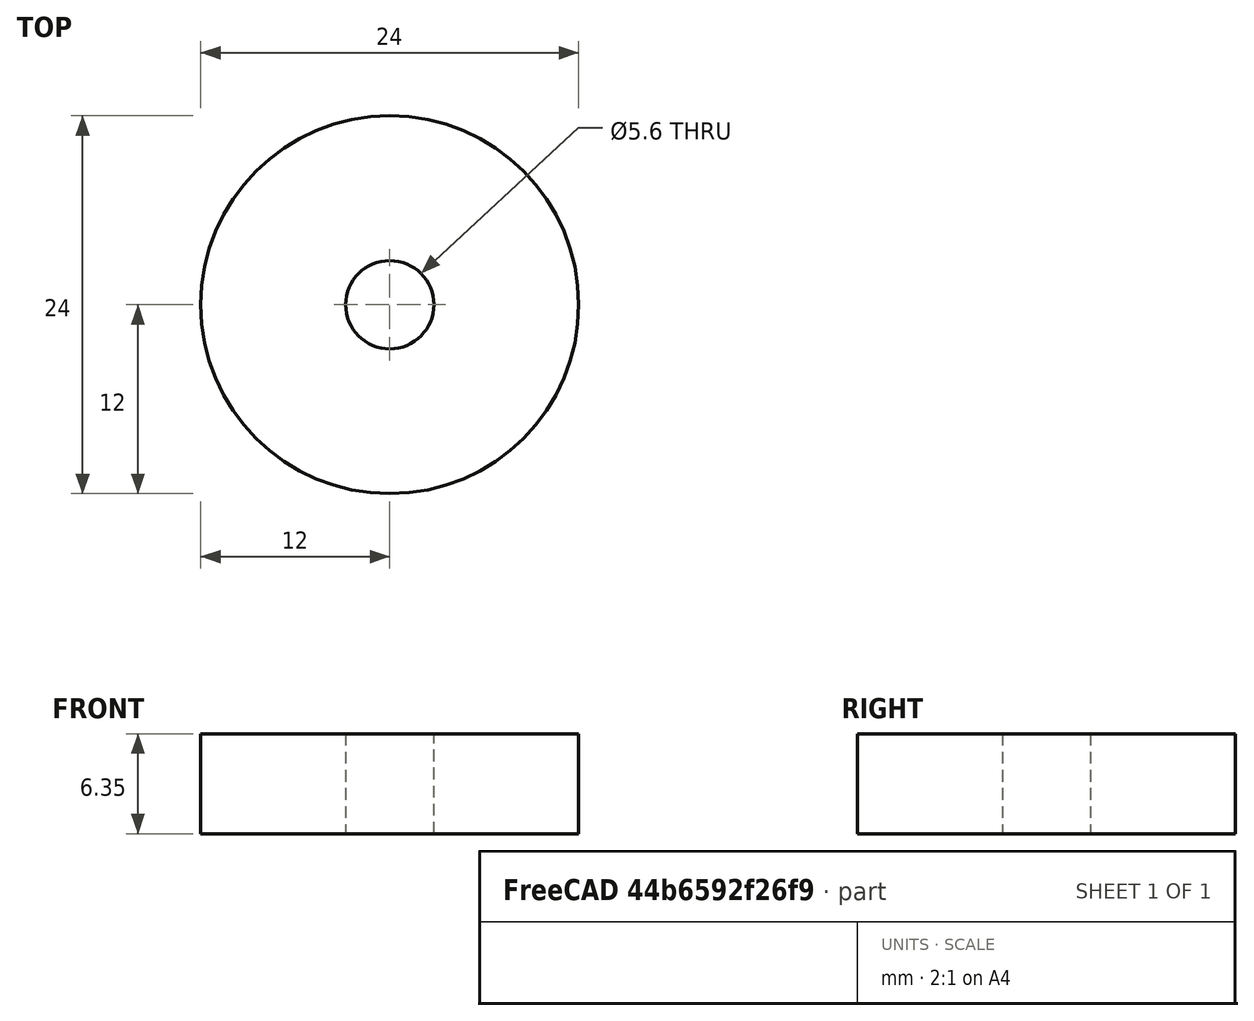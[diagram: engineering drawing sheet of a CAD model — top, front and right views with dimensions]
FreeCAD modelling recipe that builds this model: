
FCSTD DOCUMENT  (FreeCAD 0.19R)
Label: Washer
License: All rights reserved
LicenseURL: http://en.wikipedia.org/wiki/All_rights_reserved
objects: Part::Feature×2, App::DocumentObjectGroup×1, Sketcher::SketchObject×1, PartDesign::Pad×1, PartDesign::Body×1, Mesh::Feature×1
note: 6 computed .brp shape members not serialized (recipe doc carries the construction recipe); baked Part::Feature solids carry a one-line shape summary decoded from their .brp

FEATURE [Part::Feature] Circle
  shape: bbox 24 x 24 x 2e-07 mm, 0 faces, 0 solids (baked)
FEATURE [Part::Feature] Circle001
  shape: bbox 5.6 x 5.6 x 2e-07 mm, 0 faces, 0 solids (baked)
FEATURE [App::DocumentObjectGroup] _  label="0"
  Group = -> [Circle,Circle001]
FEATURE [Sketcher::SketchObject] Sketch
  FullyConstrained = false
  sketch-geometry (2):
    g0: Circle CenterX=0 CenterY=0 CenterZ=0 NormalX=0 NormalY=0 NormalZ=1 AngleXU=0 Radius=12
    g1: Circle CenterX=0 CenterY=0 CenterZ=0 NormalX=0 NormalY=0 NormalZ=1 AngleXU=0 Radius=2.8
FEATURE [PartDesign::Pad] Pad
  Direction = (1,1,1)
  Length = 6.35
  Length2 = 100
  Profile = -> Sketch
  Type = 0
FEATURE [PartDesign::Body] Body
  Group = -> [Sketch,Pad]
  Origin = -> Origin
  Tip = -> Pad
FEATURE [Mesh::Feature] Mesh  label="Pad (Meshed)"
